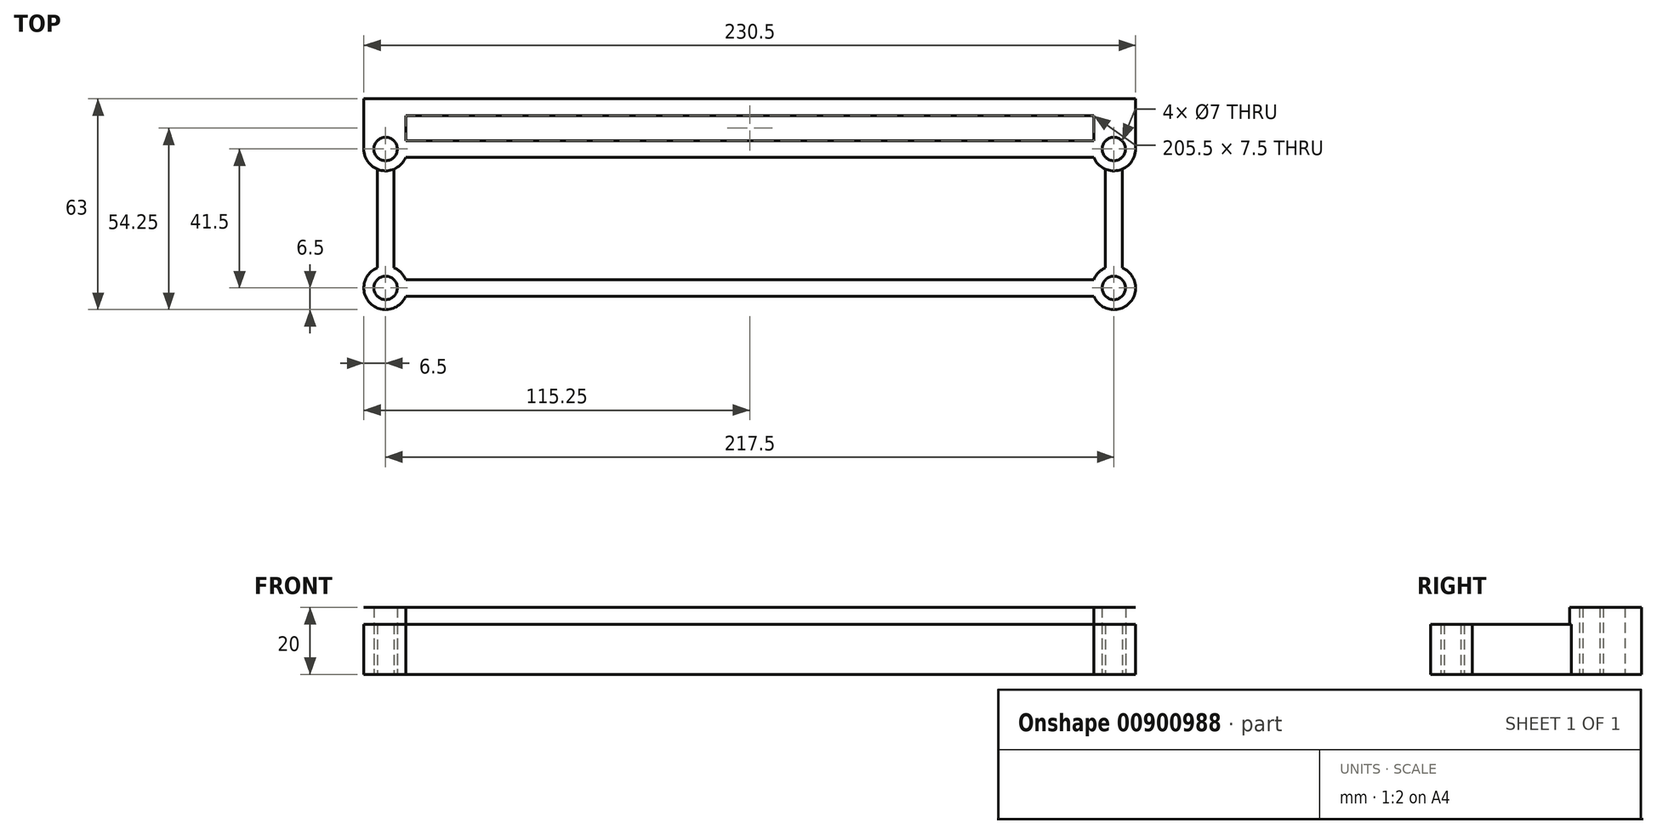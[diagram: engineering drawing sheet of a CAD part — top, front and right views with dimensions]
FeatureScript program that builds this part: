
annotation { "Feature Type Name" : "Feature", "Feature Type Description" : "" }
export const myFeature = defineFeature(function(context is Context, id is Id, definition is map)
    precondition{}
    {
        {
            var Q0;
            Q0=qCreatedBy(makeId("Top.planeOp"),FACE);
            var sketch = newSketch(context, id + "F0", { "sketchPlane" : qUnion([Q0])});
            skCircle(sketch, "E0", {"center": v(-108.75, 28.07) * mm, "radius": 3.5 * mm});
            skArc(sketch, "E1", {"start": v(-115.25, 28.07) * mm, "mid": v(-114.16, 24.46) * mm, "end": v(-111.25, 22.07) * mm});
            skCircle(sketch, "E2", {"center": v(108.75, 28.07) * mm, "radius": 3.5 * mm});
            skArc(sketch, "E3", {"start": v(102.75, 25.57) * mm, "mid": v(104.15, 23.47) * mm, "end": v(106.25, 22.07) * mm});
            skLineSegment(sketch, "E4.bottom", {"start": v(-102.75, 30.57) * mm, "end": v(102.75, 30.57) * mm});
            skLineSegment(sketch, "E4.top", {"start": v(-102.75, 25.57) * mm, "end": v(102.75, 25.57) * mm});
            skLineSegment(sketch, "E5", {"start": v(-108.75, 28.07) * mm, "end": v(-122.06, 28.07) * mm, "construction": true});
            skCircle(sketch, "E6", {"center": v(-108.75, -13.43) * mm, "radius": 3.5 * mm});
            skArc(sketch, "E7", {"start": v(-102.75, -10.93) * mm, "mid": v(-104.15, -8.83) * mm, "end": v(-106.25, -7.43) * mm});
            skCircle(sketch, "E8", {"center": v(108.75, -13.43) * mm, "radius": 3.5 * mm});
            skArc(sketch, "E9", {"start": v(102.75, -15.93) * mm, "mid": v(113.35, -18.03) * mm, "end": v(111.25, -7.43) * mm});
            skLineSegment(sketch, "E10.left", {"start": v(-111.25, 22.07) * mm, "end": v(-111.25, -7.43) * mm});
            skLineSegment(sketch, "E10.right", {"start": v(-106.25, 22.07) * mm, "end": v(-106.25, -7.43) * mm});
            skLineSegment(sketch, "E11.bottom", {"start": v(-102.75, -10.93) * mm, "end": v(102.75, -10.93) * mm});
            skLineSegment(sketch, "E11.top", {"start": v(-102.75, -15.93) * mm, "end": v(102.75, -15.93) * mm});
            skLineSegment(sketch, "E12.left", {"start": v(106.25, 22.07) * mm, "end": v(106.25, -7.43) * mm});
            skLineSegment(sketch, "E12.right", {"start": v(111.25, 22.07) * mm, "end": v(111.25, -7.43) * mm});
            skArc(sketch, "E13.trimOffspring", {"start": v(-111.25, -7.43) * mm, "mid": v(-113.35, -18.03) * mm, "end": v(-102.75, -15.93) * mm});
            skArc(sketch, "E14.trimOffspring", {"start": v(-106.25, 22.07) * mm, "mid": v(-104.15, 23.47) * mm, "end": v(-102.75, 25.57) * mm});
            skArc(sketch, "E15.trimOffspring", {"start": v(106.25, -7.43) * mm, "mid": v(104.15, -8.83) * mm, "end": v(102.75, -10.93) * mm});
            skArc(sketch, "E16.trimOffspring", {"start": v(111.25, 22.07) * mm, "mid": v(114.16, 24.46) * mm, "end": v(115.25, 28.07) * mm});
            skLineSegment(sketch, "E17", {"start": v(-115.25, 43.07) * mm, "end": v(115.25, 43.07) * mm});
            skLineSegment(sketch, "E18", {"start": v(-115.25, 28.07) * mm, "end": v(-115.25, 43.07) * mm});
            skPoint(sketch, "E19.orphan", {"position": v(-110.78, 43.07) * mm});
            skLineSegment(sketch, "E20", {"start": v(115.25, 28.07) * mm, "end": v(115.25, 43.07) * mm});
            skLineSegment(sketch, "E21", {"start": v(102.75, 30.57) * mm, "end": v(102.75, 38.07) * mm});
            skLineSegment(sketch, "E22.0", {"start": v(-102.75, 38.07) * mm, "end": v(102.75, 38.07) * mm});
            skLineSegment(sketch, "E23", {"start": v(-102.75, 30.57) * mm, "end": v(-102.75, 38.07) * mm});
            skSolve(sketch);
        }
        {
            var Q0;
            Q0=qSketchRegion(id+"F0",true);
            extrude(context, id + "F1", {"entities" : qUnion([Q0]), "depth" : 7 * mm, "offsetDistance" : 25 * mm});
        }
        {
            var Q0;
            Q0=makeQuery(id+"F1.opExtrude","CAP_FACE",FACE,{"disambiguationData":[OSD([sQuery(id+"F0.wireOp",EDGE,"E0"),sQuery(id+"F0.wireOp",EDGE,"E1"),sQuery(id+"F0.wireOp",EDGE,"E2"),sQuery(id+"F0.wireOp",EDGE,"E3"),sQuery(id+"F0.wireOp",EDGE,"E4.bottom"),sQuery(id+"F0.wireOp",EDGE,"E4.top"),sQuery(id+"F0.wireOp",EDGE,"E6"),sQuery(id+"F0.wireOp",EDGE,"E7"),sQuery(id+"F0.wireOp",EDGE,"E8"),sQuery(id+"F0.wireOp",EDGE,"E9"),sQuery(id+"F0.wireOp",EDGE,"E10.left"),sQuery(id+"F0.wireOp",EDGE,"E10.right"),sQuery(id+"F0.wireOp",EDGE,"E11.bottom"),sQuery(id+"F0.wireOp",EDGE,"E11.top"),sQuery(id+"F0.wireOp",EDGE,"E12.left"),sQuery(id+"F0.wireOp",EDGE,"E12.right"),sQuery(id+"F0.wireOp",EDGE,"E13.trimOffspring"),sQuery(id+"F0.wireOp",EDGE,"E14.trimOffspring"),sQuery(id+"F0.wireOp",EDGE,"E15.trimOffspring"),sQuery(id+"F0.wireOp",EDGE,"E16.trimOffspring"),sQuery(id+"F0.wireOp",EDGE,"E17"),sQuery(id+"F0.wireOp",EDGE,"E18"),sQuery(id+"F0.wireOp",EDGE,"E20"),sQuery(id+"F0.wireOp",EDGE,"E21"),sQuery(id+"F0.wireOp",EDGE,"E22.0"),sQuery(id+"F0.wireOp",EDGE,"E23")])],"isStart":false});
            var sketch = newSketch(context, id + "F2", { "sketchPlane" : qUnion([Q0])});
            skLineSegment(sketch, "E24.0", {"start": v(-115.25, 43.07) * mm, "end": v(115.25, 43.07) * mm});
            skLineSegment(sketch, "E25.0", {"start": v(-115.25, 28.07) * mm, "end": v(-115.25, 43.07) * mm});
            skLineSegment(sketch, "E26.0", {"start": v(-102.75, 30.57) * mm, "end": v(-102.75, 38.07) * mm});
            skLineSegment(sketch, "E27.0", {"start": v(-102.75, 30.57) * mm, "end": v(102.75, 30.57) * mm});
            skLineSegment(sketch, "E28.0", {"start": v(-102.75, 38.07) * mm, "end": v(102.75, 38.07) * mm});
            skPoint(sketch, "E29.0", {"position": v(102.75, 34.32) * mm});
            skCircle(sketch, "E30.0", {"center": v(108.75, 28.07) * mm, "radius": 3.5 * mm});
            skLineSegment(sketch, "E31.0", {"start": v(115.25, 28.07) * mm, "end": v(115.25, 43.07) * mm});
            skCircle(sketch, "E32.0", {"center": v(-108.75, 28.07) * mm, "radius": 3.5 * mm});
            skArc(sketch, "E33.0", {"start": v(-115.25, 28.07) * mm, "mid": v(-114.16, 24.46) * mm, "end": v(-111.25, 22.07) * mm});
            skArc(sketch, "E34.0", {"start": v(-106.25, 22.07) * mm, "mid": v(-104.15, 23.47) * mm, "end": v(-102.75, 25.57) * mm});
            skLineSegment(sketch, "E35.0", {"start": v(-102.75, 25.57) * mm, "end": v(102.75, 25.57) * mm});
            skArc(sketch, "E36.0", {"start": v(102.75, 25.57) * mm, "mid": v(104.15, 23.47) * mm, "end": v(106.25, 22.07) * mm});
            skArc(sketch, "E37.0", {"start": v(111.25, 22.07) * mm, "mid": v(114.16, 24.46) * mm, "end": v(115.25, 28.07) * mm});
            skArc(sketch, "E38", {"start": v(106.25, 22.07) * mm, "mid": v(108.75, 21.57) * mm, "end": v(111.25, 22.07) * mm});
            skArc(sketch, "E39", {"start": v(-111.25, 22.07) * mm, "mid": v(-108.75, 21.57) * mm, "end": v(-106.25, 22.07) * mm});
            skLineSegment(sketch, "E40", {"start": v(102.75, 30.57) * mm, "end": v(102.75, 38.07) * mm});
            skSolve(sketch);
        }
        {
            var Q0;
            Q0=qSketchRegion(id+"F2",true);
            extrude(context, id + "F3", {"entities" : qUnion([Q0]), "operationType" : NewBodyOperationType.ADD, "depth" : 5 * mm, "offsetDistance" : 25 * mm});
        }
        {
            var Q0;
            Q0=makeQuery(id+"F1.opExtrude","CAP_FACE",FACE,{"disambiguationData":[OSD([sQuery(id+"F0.wireOp",EDGE,"E0"),sQuery(id+"F0.wireOp",EDGE,"E1"),sQuery(id+"F0.wireOp",EDGE,"E2"),sQuery(id+"F0.wireOp",EDGE,"E3"),sQuery(id+"F0.wireOp",EDGE,"E4.bottom"),sQuery(id+"F0.wireOp",EDGE,"E4.top"),sQuery(id+"F0.wireOp",EDGE,"E6"),sQuery(id+"F0.wireOp",EDGE,"E7"),sQuery(id+"F0.wireOp",EDGE,"E8"),sQuery(id+"F0.wireOp",EDGE,"E9"),sQuery(id+"F0.wireOp",EDGE,"E10.left"),sQuery(id+"F0.wireOp",EDGE,"E10.right"),sQuery(id+"F0.wireOp",EDGE,"E11.bottom"),sQuery(id+"F0.wireOp",EDGE,"E11.top"),sQuery(id+"F0.wireOp",EDGE,"E12.left"),sQuery(id+"F0.wireOp",EDGE,"E12.right"),sQuery(id+"F0.wireOp",EDGE,"E13.trimOffspring"),sQuery(id+"F0.wireOp",EDGE,"E14.trimOffspring"),sQuery(id+"F0.wireOp",EDGE,"E15.trimOffspring"),sQuery(id+"F0.wireOp",EDGE,"E16.trimOffspring"),sQuery(id+"F0.wireOp",EDGE,"E17"),sQuery(id+"F0.wireOp",EDGE,"E18"),sQuery(id+"F0.wireOp",EDGE,"E20"),sQuery(id+"F0.wireOp",EDGE,"E21"),sQuery(id+"F0.wireOp",EDGE,"E22.0"),sQuery(id+"F0.wireOp",EDGE,"E23")])],"isStart":true});
            var sketch = newSketch(context, id + "F4", { "sketchPlane" : qUnion([Q0])});
            skLineSegment(sketch, "E41.0.0", {"start": v(111.25, -22.07) * mm, "end": v(111.25, 7.43) * mm});
            skArc(sketch, "E41.0.1", {"start": v(111.25, 7.43) * mm, "mid": v(113.35, 18.03) * mm, "end": v(102.75, 15.93) * mm});
            skLineSegment(sketch, "E41.0.2", {"start": v(102.75, 15.93) * mm, "end": v(-102.75, 15.93) * mm});
            skArc(sketch, "E41.0.3", {"start": v(-102.75, 15.93) * mm, "mid": v(-113.35, 18.03) * mm, "end": v(-111.25, 7.43) * mm});
            skLineSegment(sketch, "E41.0.4", {"start": v(-111.25, 7.43) * mm, "end": v(-111.25, -22.07) * mm});
            skArc(sketch, "E41.0.5", {"start": v(-111.25, -22.07) * mm, "mid": v(-114.16, -24.46) * mm, "end": v(-115.25, -28.07) * mm});
            skLineSegment(sketch, "E41.0.6", {"start": v(-115.25, -28.07) * mm, "end": v(-115.25, -43.07) * mm});
            skLineSegment(sketch, "E41.0.7", {"start": v(-115.25, -43.07) * mm, "end": v(115.25, -43.07) * mm});
            skLineSegment(sketch, "E41.0.8", {"start": v(115.25, -43.07) * mm, "end": v(115.25, -28.07) * mm});
            skArc(sketch, "E41.0.9", {"start": v(115.25, -28.07) * mm, "mid": v(114.16, -24.46) * mm, "end": v(111.25, -22.07) * mm});
            skLineSegment(sketch, "E42.0", {"start": v(-102.75, -38.07) * mm, "end": v(102.75, -38.07) * mm});
            skLineSegment(sketch, "E43.0", {"start": v(102.75, -30.57) * mm, "end": v(102.75, -38.07) * mm});
            skLineSegment(sketch, "E44.0", {"start": v(-102.75, -30.57) * mm, "end": v(102.75, -30.57) * mm});
            skCircle(sketch, "E45.0", {"center": v(108.75, -28.07) * mm, "radius": 3.5 * mm});
            skCircle(sketch, "E46.0", {"center": v(108.75, 13.43) * mm, "radius": 3.5 * mm});
            skPoint(sketch, "E47.0", {"position": v(104.15, 8.83) * mm});
            skArc(sketch, "E48.0", {"start": v(106.25, 7.43) * mm, "mid": v(104.15, 8.83) * mm, "end": v(102.75, 10.93) * mm});
            skLineSegment(sketch, "E49.0", {"start": v(-102.75, 10.93) * mm, "end": v(102.75, 10.93) * mm});
            skLineSegment(sketch, "E50.0", {"start": v(-102.75, -25.57) * mm, "end": v(102.75, -25.57) * mm});
            skArc(sketch, "E51.0", {"start": v(102.75, -25.57) * mm, "mid": v(104.15, -23.47) * mm, "end": v(106.25, -22.07) * mm});
            skLineSegment(sketch, "E52.0", {"start": v(106.25, -22.07) * mm, "end": v(106.25, 7.43) * mm});
            skCircle(sketch, "E53.0", {"center": v(-108.75, -28.07) * mm, "radius": 3.5 * mm});
            skArc(sketch, "E54.0", {"start": v(-106.25, -22.07) * mm, "mid": v(-104.15, -23.47) * mm, "end": v(-102.75, -25.57) * mm});
            skLineSegment(sketch, "E55.0", {"start": v(-106.25, -22.07) * mm, "end": v(-106.25, 7.43) * mm});
            skArc(sketch, "E56.0", {"start": v(-102.75, 10.93) * mm, "mid": v(-104.15, 8.83) * mm, "end": v(-106.25, 7.43) * mm});
            skCircle(sketch, "E57.0", {"center": v(-108.75, 13.43) * mm, "radius": 3.5 * mm});
            skLineSegment(sketch, "E58.0", {"start": v(-102.75, -30.57) * mm, "end": v(-102.75, -38.07) * mm});
            skSolve(sketch);
        }
        {
            var Q0;
            Q0=qSketchRegion(id+"F4",true);
            extrude(context, id + "F5", {"entities" : qUnion([Q0]), "operationType" : NewBodyOperationType.ADD, "depth" : 8 * mm, "offsetDistance" : 25 * mm});
        }
    });
